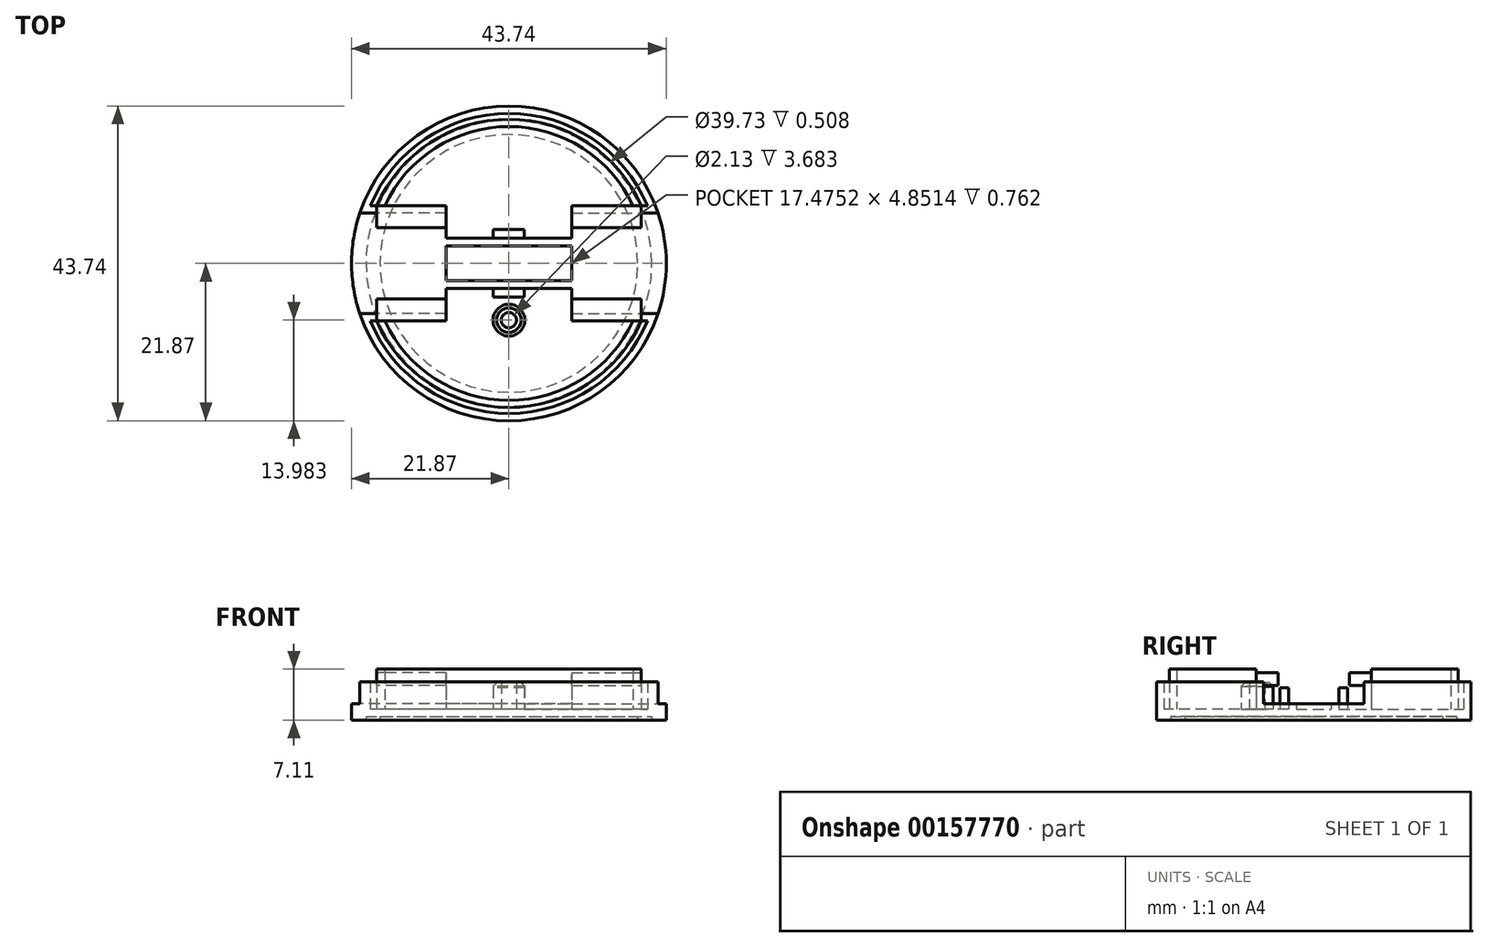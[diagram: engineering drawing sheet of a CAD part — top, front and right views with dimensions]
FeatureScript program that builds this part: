
annotation { "Feature Type Name" : "Feature", "Feature Type Description" : "" }
export const myFeature = defineFeature(function(context is Context, id is Id, definition is map)
    precondition{}
    {
        {
            var Q0;
            Q0=qCreatedBy(makeId("Front.planeOp"),FACE);
            var sketch = newSketch(context, id + "F0", { "sketchPlane" : qUnion([Q0])});
            skLineSegment(sketch, "E0", {"start": v(0, 0) * mm, "end": v(-17.9, 0) * mm});
            skLineSegment(sketch, "E1", {"start": v(-17.9, 0) * mm, "end": v(-17.9, 0.5) * mm});
            skLineSegment(sketch, "E2", {"start": v(-17.9, 0.5) * mm, "end": v(-19.86, 0.5) * mm});
            skLineSegment(sketch, "E3", {"start": v(-19.86, 0.5) * mm, "end": v(-19.86, 0) * mm});
            skLineSegment(sketch, "E4", {"start": v(-19.86, 0) * mm, "end": v(-21.87, 0) * mm});
            skLineSegment(sketch, "E5", {"start": v(-21.87, 0) * mm, "end": v(-21.87, 5.33) * mm});
            skLineSegment(sketch, "E6", {"start": v(-21.87, 5.33) * mm, "end": v(-20.85, 5.33) * mm});
            skLineSegment(sketch, "E7", {"start": v(-20.85, 5.33) * mm, "end": v(-20.85, 1.52) * mm});
            skLineSegment(sketch, "E8", {"start": v(-20.85, 1.52) * mm, "end": v(-20.04, 1.52) * mm});
            skLineSegment(sketch, "E9", {"start": v(-20.04, 1.52) * mm, "end": v(-20.04, 7.11) * mm});
            skLineSegment(sketch, "E10", {"start": v(-20.04, 7.11) * mm, "end": v(-19.02, 7.11) * mm});
            skLineSegment(sketch, "E11", {"start": v(-19.02, 7.11) * mm, "end": v(-19.02, 1.52) * mm});
            skLineSegment(sketch, "E12", {"start": v(-19.02, 1.52) * mm, "end": v(0, 1.52) * mm});
            skLineSegment(sketch, "E13", {"start": v(0, 1.52) * mm, "end": v(0, 0) * mm});
            skLineSegment(sketch, "E14", {"start": v(0, 1.52) * mm, "end": v(0, 8.98) * mm, "construction": true});
            skSolve(sketch);
        }
        {
            var Q0;
            Q0 = qSketchRegion(id + "F0", true);
            var Q1;
            Q1=sQuery(id+"F0.wireOp",EDGE,"E14");
            revolve(context, id + "F1", {"entities" : qUnion([Q0]), "axis" : qUnion([Q1]), "revolveType" : RevolveType.ONE_DIRECTION, "angle" : 90 * degree});
        }
        {
            var Q0;
            Q0=makeQuery(id+"F1.opRevolve","SWEPT_FACE",FACE,{"disambiguationData":[OSD([sQuery(id+"F0.wireOp",EDGE,"E12")])]});
            var sketch = newSketch(context, id + "F2", { "sketchPlane" : qUnion([Q0])});
            skLineSegment(sketch, "E15", {"start": v(0, -2.43) * mm, "end": v(-8.74, -2.43) * mm});
            skLineSegment(sketch, "E16", {"start": v(-8.74, -2.43) * mm, "end": v(-8.74, 0) * mm});
            skLineSegment(sketch, "E17", {"start": v(0, -2.43) * mm, "end": v(0, -3.5) * mm});
            skLineSegment(sketch, "E18", {"start": v(0, -3.5) * mm, "end": v(-8.74, -3.5) * mm});
            skLineSegment(sketch, "E19", {"start": v(-8.74, -3.5) * mm, "end": v(-8.74, -8.01) * mm});
            skLineSegment(sketch, "E20", {"start": v(-8.74, -8.01) * mm, "end": v(-20.35, -8.01) * mm});
            skLineSegment(sketch, "E21", {"start": v(-21.87, 0) * mm, "end": v(-8.74, 0) * mm});
            skArc(sketch, "E22.0", {"start": v(-20.35, -8.01) * mm, "mid": v(-21.49, -4.08) * mm, "end": v(-21.87, 0) * mm});
            skPoint(sketch, "E23.orphan", {"position": v(0, -21.87) * mm});
            skLineSegment(sketch, "E24", {"start": v(-8.74, 0) * mm, "end": v(9.15, 0) * mm, "construction": true});
            skSolve(sketch);
        }
        {
            var Q0;
            Q0 = qSketchRegion(id + "F2", true);
            extrude(context, id + "F3", {"entities" : qUnion([Q0]), "operationType" : NewBodyOperationType.REMOVE, "depth" : 25.4 * mm});
        }
        {
            var Q0;
            Q0 = qSketchRegion(id + "F2", true);
            extrude(context, id + "F4", {"entities" : qUnion([Q0]), "operationType" : NewBodyOperationType.ADD, "depth" : 0.76 * mm});
        }
        {
            var Q0;
            Q0=makeQuery(id+"F4.opExtrude","CAP_FACE",FACE,{"disambiguationData":[OSD([sQuery(id+"F2.wireOp",EDGE,"E15"),sQuery(id+"F2.wireOp",EDGE,"E16"),sQuery(id+"F2.wireOp",EDGE,"E17"),sQuery(id+"F2.wireOp",EDGE,"E18"),sQuery(id+"F2.wireOp",EDGE,"E19"),sQuery(id+"F2.wireOp",EDGE,"E20"),sQuery(id+"F2.wireOp",EDGE,"E21"),sQuery(id+"F2.wireOp",EDGE,"E22.0")])],"isStart":false});
            var sketch = newSketch(context, id + "F5", { "sketchPlane" : qUnion([Q0])});
            skLineSegment(sketch, "E25", {"start": v(-8.74, -8.01) * mm, "end": v(-8.74, -7) * mm});
            skLineSegment(sketch, "E26", {"start": v(-8.74, -7) * mm, "end": v(-20.72, -7) * mm});
            skLineSegment(sketch, "E27", {"start": v(-8.74, -8.01) * mm, "end": v(-20.35, -8.01) * mm});
            skArc(sketch, "E28.0", {"start": v(-20.35, -8.01) * mm, "mid": v(-20.54, -7.5) * mm, "end": v(-20.72, -7) * mm});
            skSolve(sketch);
        }
        {
            var Q0;
            Q0 = qSketchRegion(id + "F5", true);
            var Q1;
            Q1=makeQuery(id+"F1.opRevolve","SWEPT_FACE",FACE,{"disambiguationData":[OSD([sQuery(id+"F0.wireOp",EDGE,"E6")])]});
            extrude(context, id + "F6", {"entities" : qUnion([Q0]), "operationType" : NewBodyOperationType.ADD, "endBound" : BoundingType.UP_TO_SURFACE, "endBoundEntityFace" : qUnion([Q1]), "depth" : 25.4 * mm});
        }
        {
            var Q0;
            {var subQ2=sQuery(id+"F2.wireOp",EDGE,"E20");var subQ10=makeQuery(id+"F1.opRevolve","SWEPT_FACE",FACE,{"disambiguationData":[OSD([sQuery(id+"F0.wireOp",EDGE,"E11")])]});Q0=makeQuery(id+"F6.boolean.opBoolean","MERGE",FACE,{"derivedFrom":[makeQuery(id+"F4.boolean.opBoolean","SPLIT",FACE,{"disambiguationData":[TD([subQ10])],"derivedFrom":makeQuery(id+"F4.opExtrude","SWEPT_FACE",FACE,{"disambiguationData":[OSD([subQ2])]})}),makeQuery(id+"F6.opExtrude","SWEPT_FACE",FACE,{"disambiguationData":[OSD([sQuery(id+"F5.wireOp",EDGE,"E27")])]})]});}
            var sketch = newSketch(context, id + "F7", { "sketchPlane" : qUnion([Q0])});
            skLineSegment(sketch, "E29.bottom", {"start": v(-8.74, 4.83) * mm, "end": v(-18.37, 4.83) * mm});
            skLineSegment(sketch, "E29.top", {"start": v(-8.74, 6.6) * mm, "end": v(-18.37, 6.6) * mm});
            skLineSegment(sketch, "E29.left", {"start": v(-8.74, 4.83) * mm, "end": v(-8.74, 6.6) * mm});
            skLineSegment(sketch, "E29.right", {"start": v(-18.37, 4.83) * mm, "end": v(-18.37, 6.6) * mm});
            skSolve(sketch);
        }
        {
            var Q0;
            Q0 = qSketchRegion(id + "F7", true);
            extrude(context, id + "F8", {"entities" : qUnion([Q0]), "operationType" : NewBodyOperationType.ADD, "oppositeDirection" : true, "depth" : 3.05 * mm});
        }
        {
            var Q0;
            {var subQ0=sQuery(id+"F2.wireOp",EDGE,"E18");var subQ1=sQuery(id+"F2.wireOp",EDGE,"E17");var subQ2=sQuery(id+"F0.wireOp",EDGE,"E11");var subQ3=sQuery(id+"F0.wireOp",EDGE,"E12");var subQ4=sQuery(id+"F0.wireOp",EDGE,"E8");var subQ5=sQuery(id+"F2.wireOp",EDGE,"E19");var subQ6=sQuery(id+"F2.wireOp",EDGE,"E20");Q0=makeQuery(id+"F4.boolean.opBoolean","SPLIT",FACE,{"disambiguationData":[TD([makeQuery(id+"F1.opRevolve","SWEPT_FACE",FACE,{"disambiguationData":[OSD([subQ2])]})])],"derivedFrom":makeQuery(id+"F3.boolean.opBoolean","MERGE",FACE,{"derivedFrom":[makeQuery(id+"F1.opRevolve","SWEPT_FACE",FACE,{"disambiguationData":[OSD([subQ4])]}),makeQuery(id+"F1.opRevolve","SWEPT_FACE",FACE,{"disambiguationData":[OSD([subQ3])]}),makeQuery(id+"F3.opExtrude","CAP_FACE",FACE,{"disambiguationData":[OSD([sQuery(id+"F2.wireOp",EDGE,"E15"),sQuery(id+"F2.wireOp",EDGE,"E16"),subQ1,subQ0,subQ5,subQ6,sQuery(id+"F2.wireOp",EDGE,"E21"),sQuery(id+"F2.wireOp",EDGE,"E22.0")])],"isStart":true})]})});}
            var sketch = newSketch(context, id + "F9", { "sketchPlane" : qUnion([Q0])});
            skLineSegment(sketch, "E30.bottom", {"start": v(0, -3.5) * mm, "end": v(-2.16, -3.5) * mm});
            skLineSegment(sketch, "E30.top", {"start": v(0, -4.7) * mm, "end": v(-2.16, -4.7) * mm});
            skLineSegment(sketch, "E30.left", {"start": v(0, -3.5) * mm, "end": v(0, -4.7) * mm});
            skLineSegment(sketch, "E30.right", {"start": v(-2.16, -3.5) * mm, "end": v(-2.16, -4.7) * mm});
            skLineSegment(sketch, "E31", {"start": v(0, 0) * mm, "end": v(0, 9.43) * mm, "construction": true});
            skLineSegment(sketch, "E32", {"start": v(0, 0) * mm, "end": v(8.36, 0) * mm, "construction": true});
            skSolve(sketch);
        }
        {
            var Q0;
            Q0 = qSketchRegion(id + "F9", true);
            extrude(context, id + "F10", {"entities" : qUnion([Q0]), "operationType" : NewBodyOperationType.ADD, "depth" : 3 * mm});
        }
        {
            var Q0;
            Q0=makeQuery(id+"F1.opRevolve","SWEPT_BODY",BODY,{"disambiguationData":[OSD([sQuery(id+"F0.wireOp",EDGE,"E0"),sQuery(id+"F0.wireOp",EDGE,"E1"),sQuery(id+"F0.wireOp",EDGE,"E2"),sQuery(id+"F0.wireOp",EDGE,"E3"),sQuery(id+"F0.wireOp",EDGE,"E4"),sQuery(id+"F0.wireOp",EDGE,"E5"),sQuery(id+"F0.wireOp",EDGE,"E6"),sQuery(id+"F0.wireOp",EDGE,"E7"),sQuery(id+"F0.wireOp",EDGE,"E8"),sQuery(id+"F0.wireOp",EDGE,"E9"),sQuery(id+"F0.wireOp",EDGE,"E10"),sQuery(id+"F0.wireOp",EDGE,"E11"),sQuery(id+"F0.wireOp",EDGE,"E12"),sQuery(id+"F0.wireOp",EDGE,"E13")])]});
            var Q1;
            Q1=makeQuery(id+"F10.boolean.opBoolean","MERGE",FACE,{"derivedFrom":[makeQuery(id+"F4.boolean.opBoolean","MERGE",FACE,{"derivedFrom":[makeQuery(id+"F1.opRevolve","CAP_FACE",FACE,{"disambiguationData":[OSD([sQuery(id+"F0.wireOp",EDGE,"E0"),sQuery(id+"F0.wireOp",EDGE,"E1"),sQuery(id+"F0.wireOp",EDGE,"E2"),sQuery(id+"F0.wireOp",EDGE,"E3"),sQuery(id+"F0.wireOp",EDGE,"E4"),sQuery(id+"F0.wireOp",EDGE,"E5"),sQuery(id+"F0.wireOp",EDGE,"E6"),sQuery(id+"F0.wireOp",EDGE,"E7"),sQuery(id+"F0.wireOp",EDGE,"E8"),sQuery(id+"F0.wireOp",EDGE,"E9"),sQuery(id+"F0.wireOp",EDGE,"E10"),sQuery(id+"F0.wireOp",EDGE,"E11"),sQuery(id+"F0.wireOp",EDGE,"E12"),sQuery(id+"F0.wireOp",EDGE,"E13")])],"isStart":false}),makeQuery(id+"F4.opExtrude","SWEPT_FACE",FACE,{"disambiguationData":[OSD([sQuery(id+"F2.wireOp",EDGE,"E17")])]})]}),makeQuery(id+"F10.opExtrude","SWEPT_FACE",FACE,{"disambiguationData":[OSD([sQuery(id+"F9.wireOp",EDGE,"E30.left")])]})]});
            mirror(context, id + "F11", {"operationType" : NewBodyOperationType.ADD, "entities" : qUnion([Q0]), "mirrorPlane" : qUnion([Q1])});
        }
        {
            var Q0;
            Q0=makeQuery(id+"F1.opRevolve","SWEPT_BODY",BODY,{"disambiguationData":[OSD([sQuery(id+"F0.wireOp",EDGE,"E0"),sQuery(id+"F0.wireOp",EDGE,"E1"),sQuery(id+"F0.wireOp",EDGE,"E2"),sQuery(id+"F0.wireOp",EDGE,"E3"),sQuery(id+"F0.wireOp",EDGE,"E4"),sQuery(id+"F0.wireOp",EDGE,"E5"),sQuery(id+"F0.wireOp",EDGE,"E6"),sQuery(id+"F0.wireOp",EDGE,"E7"),sQuery(id+"F0.wireOp",EDGE,"E8"),sQuery(id+"F0.wireOp",EDGE,"E9"),sQuery(id+"F0.wireOp",EDGE,"E10"),sQuery(id+"F0.wireOp",EDGE,"E11"),sQuery(id+"F0.wireOp",EDGE,"E12"),sQuery(id+"F0.wireOp",EDGE,"E13")])]});
            var Q1;
            {var subQ0=makeQuery(id+"F4.boolean.opBoolean","MERGE",FACE,{"derivedFrom":[makeQuery(id+"F1.opRevolve","CAP_FACE",FACE,{"disambiguationData":[OSD([sQuery(id+"F0.wireOp",EDGE,"E0"),sQuery(id+"F0.wireOp",EDGE,"E1"),sQuery(id+"F0.wireOp",EDGE,"E2"),sQuery(id+"F0.wireOp",EDGE,"E3"),sQuery(id+"F0.wireOp",EDGE,"E4"),sQuery(id+"F0.wireOp",EDGE,"E5"),sQuery(id+"F0.wireOp",EDGE,"E6"),sQuery(id+"F0.wireOp",EDGE,"E7"),sQuery(id+"F0.wireOp",EDGE,"E8"),sQuery(id+"F0.wireOp",EDGE,"E9"),sQuery(id+"F0.wireOp",EDGE,"E10"),sQuery(id+"F0.wireOp",EDGE,"E11"),sQuery(id+"F0.wireOp",EDGE,"E12"),sQuery(id+"F0.wireOp",EDGE,"E13")])],"isStart":true}),makeQuery(id+"F4.opExtrude","SWEPT_FACE",FACE,{"disambiguationData":[OSD([sQuery(id+"F2.wireOp",EDGE,"E21")])]})]});Q1=makeQuery(id+"F11.boolean.opBoolean","MERGE",FACE,{"derivedFrom":[subQ0,makeQuery(id+"F11.opPattern","COPY",FACE,{"derivedFrom":subQ0,"instanceName":"1"})]});}
            mirror(context, id + "F12", {"operationType" : NewBodyOperationType.ADD, "entities" : qUnion([Q0]), "mirrorPlane" : qUnion([Q1])});
        }
        {
            var Q0;
            {var subQ0=sQuery(id+"F2.wireOp",EDGE,"E18");var subQ1=sQuery(id+"F2.wireOp",EDGE,"E17");var subQ2=sQuery(id+"F0.wireOp",EDGE,"E11");var subQ3=sQuery(id+"F0.wireOp",EDGE,"E12");var subQ4=sQuery(id+"F0.wireOp",EDGE,"E8");var subQ5=sQuery(id+"F2.wireOp",EDGE,"E19");var subQ6=sQuery(id+"F2.wireOp",EDGE,"E20");var subQ7=makeQuery(id+"F4.boolean.opBoolean","SPLIT",FACE,{"disambiguationData":[TD([makeQuery(id+"F1.opRevolve","SWEPT_FACE",FACE,{"disambiguationData":[OSD([subQ2])]})])],"derivedFrom":makeQuery(id+"F3.boolean.opBoolean","MERGE",FACE,{"derivedFrom":[makeQuery(id+"F1.opRevolve","SWEPT_FACE",FACE,{"disambiguationData":[OSD([subQ4])]}),makeQuery(id+"F1.opRevolve","SWEPT_FACE",FACE,{"disambiguationData":[OSD([subQ3])]}),makeQuery(id+"F3.opExtrude","CAP_FACE",FACE,{"disambiguationData":[OSD([sQuery(id+"F2.wireOp",EDGE,"E15"),sQuery(id+"F2.wireOp",EDGE,"E16"),subQ1,subQ0,subQ5,subQ6,sQuery(id+"F2.wireOp",EDGE,"E21"),sQuery(id+"F2.wireOp",EDGE,"E22.0")])],"isStart":true})]})});Q0=makeQuery(id+"F11.boolean.opBoolean","MERGE",FACE,{"derivedFrom":[subQ7,makeQuery(id+"F11.opPattern","COPY",FACE,{"derivedFrom":subQ7,"instanceName":"1"})]});}
            var sketch = newSketch(context, id + "F13", { "sketchPlane" : qUnion([Q0])});
            skCircle(sketch, "E33", {"center": v(0, -7.89) * mm, "radius": 2.2 * mm});
            skCircle(sketch, "E34", {"center": v(0, -7.89) * mm, "radius": 1.07 * mm});
            skSolve(sketch);
        }
        {
            var Q0;
            Q0 = qSketchRegion(id + "F13", true);
            extrude(context, id + "F14", {"entities" : qUnion([Q0]), "operationType" : NewBodyOperationType.ADD, "depth" : 3.68 * mm});
        }
        {
            var Q0;
            Q0=makeQuery(id+"F14.opExtrude","CAP_EDGE",EDGE,{"disambiguationData":[OSD([sQuery(id+"F13.wireOp",EDGE,"E33")])],"isStart":false});
            chamfer(context, id + "F15", {"entities" : qUnion([Q0]), "width" : 0.5 * mm, "tangentPropagation" : true});
        }
    });
